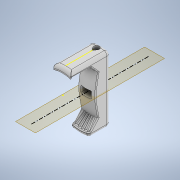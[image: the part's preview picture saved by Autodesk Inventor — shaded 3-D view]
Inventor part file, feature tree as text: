
AUTODESK INVENTOR PART (.ipt)
format: ipt  version: 2022 (Build 260153000, 153)  size: 633,856 bytes
history: native  units: mm
features: sketch x12, fillet x10, extrude x9, projected_geometry x5, other x5, plane x3, reference x2, revolve x1, pattern_circular x1, mirror x1
ambient origin geometry x8: Origin, YZ Plane, XZ Plane, XY Plane, X Axis, Y Axis, Z Axis, Center Point
bodies: Solid1 (feature_tree)
feature tree (49):
  plane  "Work Plane1"
  extrude  "Extrusion1"  Depth=20.0mm
  revolve  "Revolution1"  [1 undecoded]
  extrude  "Extrusion2"  Depth=10.0mm TaperAngle=0.0deg
  extrude  "Extrusion3"  TaperAngle=0.0deg  [1 undecoded]
  extrude  "Extrusion4"  TaperAngle=0.0deg  [1 undecoded]
  extrude  "Extrusion5"  Depth=1.0mm TaperAngle=0.0deg
  fillet  "Fillet1"  Radius=6.0mm
  fillet  "Fillet2"  Radius=2.0mm
  fillet  "Fillet3"  Radius=2.0mm
  fillet  "Fillet4"  Radius=4.0mm
  fillet  "Fillet6"  Radius=4.0mm
  fillet  "Fillet7"  Radius=1.0mm
  fillet  "Fillet8"  Radius=0.5mm
  extrude  "Extrusion6"  Depth=12.2mm
  fillet  "Fillet9"  Radius=8.2mm
  sketch  "Sketch8"  dims[d28=8.2mm d29=0.0mm d30=1.0mm]
  plane  "Work Plane3"
  extrude  "Extrusion7"  Depth=1.0mm
  extrude  "Extrusion8"  Depth=1.0mm
  sketch  "Sketch12"  dims[d37=10.0mm d38=0.0mm d39=50.0mm d40=4.48799mm]
  pattern_circular  "Circular Pattern1"  Count=5  [1 undecoded]
  plane  "Work Plane4"
  mirror  "Mirror1"
  extrude  "Extrusion9"  TaperAngle=0.0deg  [1 undecoded]
  fillet  "Fillet10"  Radius=0.5mm
  fillet  "Fillet11"  Radius=0.5mm
  sketch  "Sketch1"  dims[d0=5.0mm d1=20.0mm]
  reference  "Reference1"
  reference  "Reference2"
  sketch  "Sketch2"  dims[d2=35.0mm d3=0.0mm d4=0.2mm]
  sketch  "Sketch3"  dims[d5=90.0deg d6=10.0mm d7=0.0mm]
  projected_geometry  "Projected Loop1"
  sketch  "Sketch4"  dims[d8=6.2mm d9=0.0mm d10=0.0mm]
  sketch  "Sketch5"  dims[d11=3.0mm d12=0.0mm d13=0.0mm]
  sketch  "Sketch6"  dims[d14=1.0mm d15=1.0mm d16=0.0mm d17=6.0mm d18=2.0mm d19=2.0mm d20=4.0mm d21=4.0mm d23=1.0mm d24=0.5mm]
  projected_geometry  "Projected Loop2"
  sketch  "Sketch7"  dims[d25=0.5mm d26=12.2mm d27=8.2mm]
  projected_geometry  "Projected Loop3"
  sketch  "Sketch10"  dims[d33=90.0deg d34=1.0mm]
  sketch  "Sketch11"  dims[d35=10.0mm d36=0.0mm]
  projected_geometry  "Projected Loop4"
  projected_geometry  "Projected Loop5"
  sketch  "Sketch13"  dims[d42=12.217305mm d43=0.0mm d44=0.0mm d45=0.5mm d46=0.5mm]
  other  "<userpath>\Documents\Inventor\etchasketch\etchasketch.iam"
  other  "etchasketch.iam"
  other  "Knobass:2"
  other  "Part4:1"
  other  "knob:1"
note: 5 required parameter values undecoded (feature->parameter linkage not recoverable at this tier; creation-order binding heuristic only, values carry confidence <= 0.55)